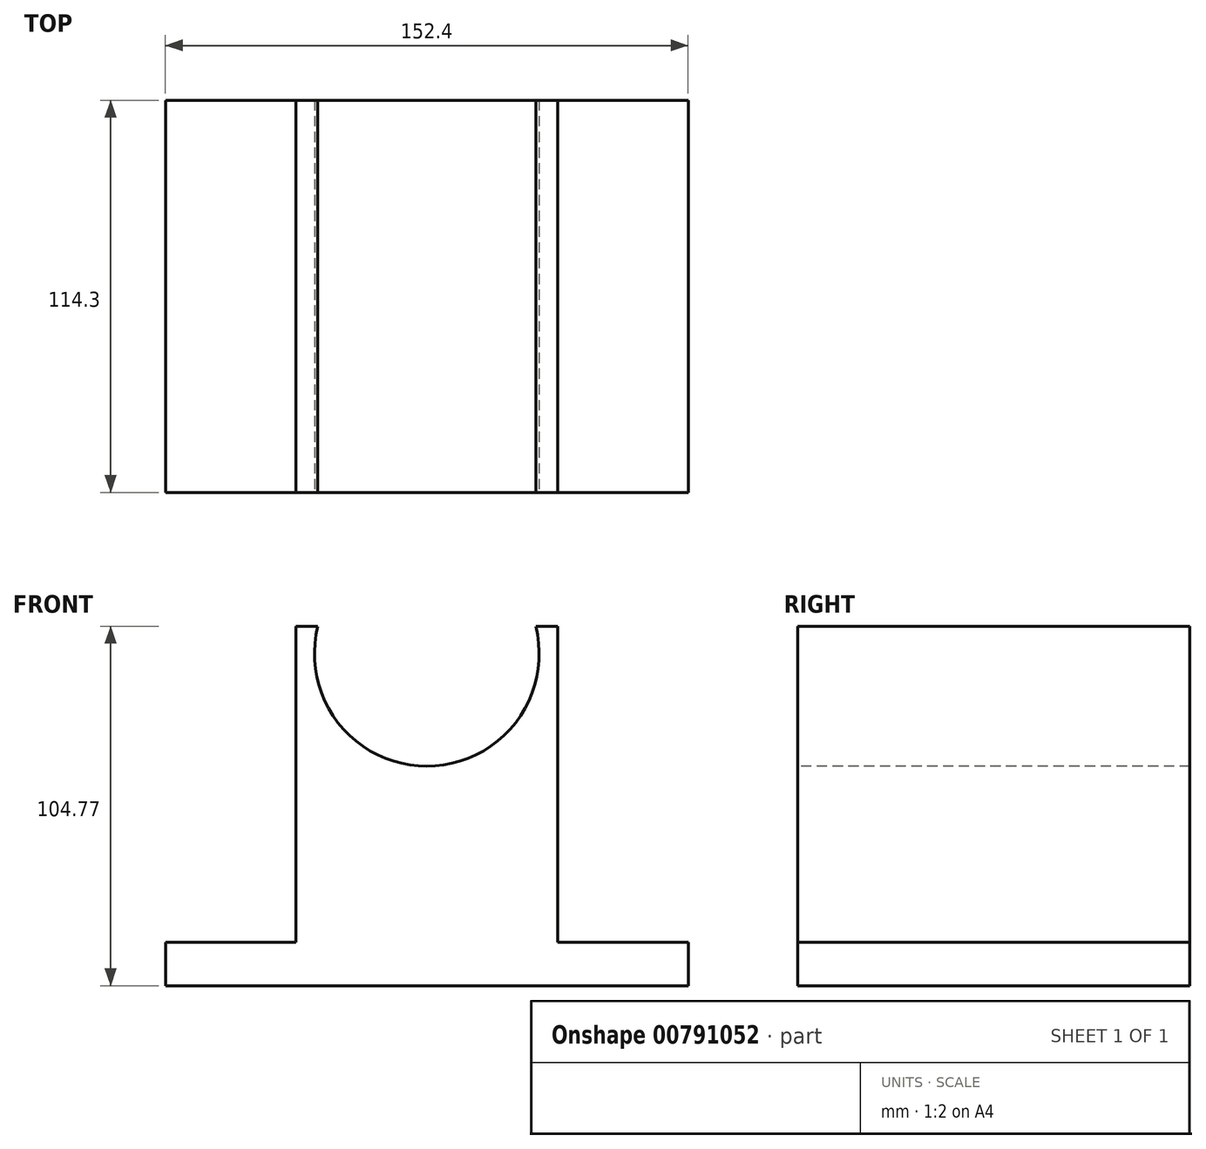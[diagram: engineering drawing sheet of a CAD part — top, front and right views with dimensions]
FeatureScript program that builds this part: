
annotation { "Feature Type Name" : "Feature", "Feature Type Description" : "" }
export const myFeature = defineFeature(function(context is Context, id is Id, definition is map)
    precondition{}
    {
        {
            var Q0;
            Q0=qCreatedBy(makeId("Front.planeOp"),FACE);
            var sketch = newSketch(context, id + "F0", { "sketchPlane" : qUnion([Q0])});
            skLineSegment(sketch, "E0", {"start": v(-75.77, 0) * mm, "end": v(76.63, 0) * mm});
            skLineSegment(sketch, "E1", {"start": v(76.63, 0) * mm, "end": v(76.63, 12.7) * mm});
            skLineSegment(sketch, "E2", {"start": v(76.63, 12.7) * mm, "end": v(38.53, 12.7) * mm});
            skLineSegment(sketch, "E3", {"start": v(-75.77, 0) * mm, "end": v(-75.77, 12.7) * mm});
            skLineSegment(sketch, "E4", {"start": v(-75.77, 12.7) * mm, "end": v(-37.67, 12.7) * mm});
            skLineSegment(sketch, "E5", {"start": v(-37.67, 12.7) * mm, "end": v(-37.67, 104.78) * mm});
            skLineSegment(sketch, "E6", {"start": v(-37.67, 104.78) * mm, "end": v(38.53, 104.78) * mm});
            skLineSegment(sketch, "E7", {"start": v(38.53, 104.78) * mm, "end": v(38.53, 12.7) * mm});
            skSolve(sketch);
        }
        {
            var Q0;
            Q0 = qSketchRegion(id + "F0", true);
            extrude(context, id + "F1", {"entities" : qUnion([Q0]), "depth" : 114.3 * mm, "offsetDistance" : 25.4 * mm});
        }
        {
            var Q0;
            Q0=makeQuery(id+"F1.opExtrude","CAP_FACE",FACE,{"disambiguationData":[OSD([sQuery(id+"F0.wireOp",EDGE,"E0"),sQuery(id+"F0.wireOp",EDGE,"E1"),sQuery(id+"F0.wireOp",EDGE,"E2"),sQuery(id+"F0.wireOp",EDGE,"E3"),sQuery(id+"F0.wireOp",EDGE,"E4"),sQuery(id+"F0.wireOp",EDGE,"E5"),sQuery(id+"F0.wireOp",EDGE,"E6"),sQuery(id+"F0.wireOp",EDGE,"E7")])],"isStart":false});
            var sketch = newSketch(context, id + "F2", { "sketchPlane" : qUnion([Q0])});
            skLineSegment(sketch, "E8", {"start": v(38.53, 104.78) * mm, "end": v(32.18, 104.78) * mm, "construction": true});
            skLineSegment(sketch, "E9", {"start": v(-37.67, 104.78) * mm, "end": v(-31.32, 104.78) * mm, "construction": true});
            skArc(sketch, "E10", {"start": v(-31.32, 104.78) * mm, "mid": v(0.43, 63.98) * mm, "end": v(32.18, 104.77) * mm});
            skLineSegment(sketch, "E11", {"start": v(-31.32, 104.78) * mm, "end": v(32.18, 104.78) * mm});
            skSolve(sketch);
        }
        {
            var Q0;
            Q0=makeQuery(id+"F2.imprint","IMPRINT",FACE,{"disambiguationData":[TD([[makeQuery(id+"F2.imprint","IMPRINT",EDGE,{"derivedFrom":sQuery(id+"F2.wireOp",EDGE,"E10")}),1.0]])]});
            extrude(context, id + "F3", {"entities" : qUnion([Q0]), "operationType" : NewBodyOperationType.REMOVE, "oppositeDirection" : true, "depth" : 114.3 * mm, "offsetDistance" : 25.4 * mm});
        }
    });
